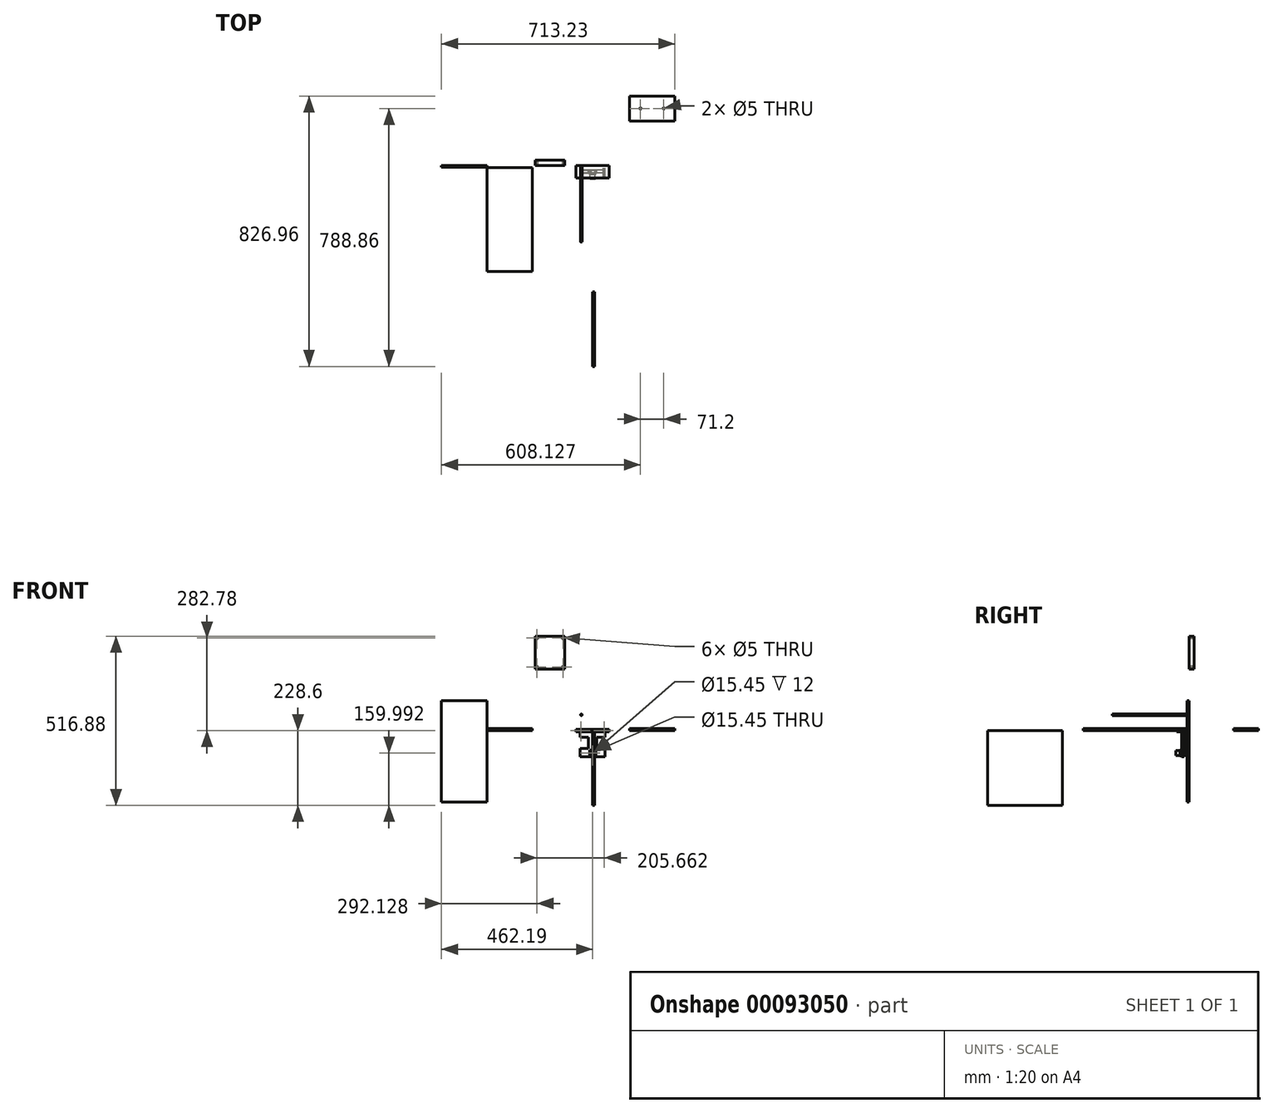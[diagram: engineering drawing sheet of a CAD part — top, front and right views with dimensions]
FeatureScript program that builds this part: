
annotation { "Feature Type Name" : "Feature", "Feature Type Description" : "" }
export const myFeature = defineFeature(function(context is Context, id is Id, definition is map)
    precondition{}
    {
        {
            var Q0;
            Q0=qCreatedBy(makeId("Front.planeOp"),FACE);
            var sketch = newSketch(context, id + "F0", { "sketchPlane" : qUnion([Q0])});
            skLineSegment(sketch, "E0.bottom", {"start": v(-50.8, -4) * mm, "end": v(50.8, -4) * mm});
            skLineSegment(sketch, "E0.top", {"start": v(-50.8, 4) * mm, "end": v(50.8, 4) * mm});
            skLineSegment(sketch, "E0.left", {"start": v(-50.8, -4) * mm, "end": v(-50.8, 4) * mm});
            skLineSegment(sketch, "E0.right", {"start": v(50.8, -4) * mm, "end": v(50.8, 4) * mm});
            skPoint(sketch, "E0.middle", {"position": v(0, 0) * mm});
            skCircle(sketch, "E1", {"center": v(-35.6, 0) * mm, "radius": 2.5 * mm});
            skCircle(sketch, "E2", {"center": v(35.6, 0) * mm, "radius": 2.5 * mm});
            skSolve(sketch);
        }
        {
            var Q0;
            Q0=qSketchRegion(id+"F0",true);
            extrude(context, id + "F1", {"entities" : qUnion([Q0]), "depth" : 38.1 * mm});
        }
        {
            var Q0;
            Q0=qCreatedBy(makeId("Front.planeOp"),FACE);
            var sketch = newSketch(context, id + "F2", { "sketchPlane" : qUnion([Q0])});
            skCircle(sketch, "E3", {"center": v(-34.4, 48.2) * mm, "radius": 2.5 * mm});
            skSolve(sketch);
        }
        {
            var Q0;
            Q0=makeQuery(id+"F2.imprint","IMPRINT",FACE,{"disambiguationData":[TD([[makeQuery(id+"F2.imprint","IMPRINT",EDGE,{"derivedFrom":sQuery(id+"F2.wireOp",EDGE,"E3")}),1.0]])]});
            extrude(context, id + "F3", {"entities" : qUnion([Q0]), "depth" : 228.6 * mm + 6 * mm});
        }
        {
            var Q0;
            Q0=qCreatedBy(makeId("Right.planeOp"),FACE);
            var sketch = newSketch(context, id + "F4", { "sketchPlane" : qUnion([Q0])});
            skLineSegment(sketch, "E4.bottom", {"start": v(-386.33, 0) * mm, "end": v(-691.13, 0) * mm});
            skLineSegment(sketch, "E4.top", {"start": v(-386.33, -304.8) * mm, "end": v(-691.13, -304.8) * mm});
            skLineSegment(sketch, "E4.left", {"start": v(-386.33, 0) * mm, "end": v(-386.33, -304.8) * mm});
            skLineSegment(sketch, "E4.right", {"start": v(-691.13, 0) * mm, "end": v(-691.13, -304.8) * mm});
            skPoint(sketch, "E4.middle", {"position": v(-538.73, -152.4) * mm});
            skLineSegment(sketch, "E5.bottom", {"start": v(-386.33, -228.6) * mm, "end": v(-614.93, -228.6) * mm});
            skLineSegment(sketch, "E5.top", {"start": v(-386.33, 0) * mm, "end": v(-614.93, 0) * mm});
            skLineSegment(sketch, "E5.left", {"start": v(-386.33, -228.6) * mm, "end": v(-386.33, 0) * mm});
            skLineSegment(sketch, "E5.right", {"start": v(-614.93, -228.6) * mm, "end": v(-614.93, 0) * mm});
            skPoint(sketch, "E5.middle", {"position": v(-500.63, -114.3) * mm});
            skSolve(sketch);
        }
        {
            var Q0;
            Q0=makeQuery(id+"F4.imprint","IMPRINT",FACE,{"disambiguationData":[TD([[makeQuery(id+"F4.imprint","IMPRINT",EDGE,{"derivedFrom":sQuery(id+"F4.wireOp",EDGE,"E4.bottom")}),1.0]])]});
            extrude(context, id + "F5", {"entities" : qUnion([Q0]), "depth" : 6 * mm});
        }
        {
            var Q0;
            Q0=qCreatedBy(makeId("Front.planeOp"),FACE);
            var sketch = newSketch(context, id + "F6", { "sketchPlane" : qUnion([Q0])});
            skLineSegment(sketch, "E6.bottom", {"start": v(-462.2, 91.62) * mm, "end": v(-323.2, 91.62) * mm});
            skLineSegment(sketch, "E6.top", {"start": v(-462.2, -219.18) * mm, "end": v(-323.2, -219.18) * mm});
            skLineSegment(sketch, "E6.left", {"start": v(-462.2, 91.62) * mm, "end": v(-462.2, -219.18) * mm});
            skLineSegment(sketch, "E6.right", {"start": v(-323.2, 91.62) * mm, "end": v(-323.2, -219.18) * mm});
            skPoint(sketch, "E6.middle", {"position": v(-392.7, -63.78) * mm});
            skSolve(sketch);
        }
        {
            var Q0;
            Q0 = qSketchRegion(id + "F6", true);
            extrude(context, id + "F7", {"entities" : qUnion([Q0]), "depth" : 6 * mm});
        }
        {
            var Q0;
            Q0=qCreatedBy(makeId("Top.planeOp"),FACE);
            var sketch = newSketch(context, id + "F8", { "sketchPlane" : qUnion([Q0])});
            skLineSegment(sketch, "E7.bottom", {"start": v(-184.06, -7.03) * mm, "end": v(-323.06, -7.03) * mm});
            skLineSegment(sketch, "E7.top", {"start": v(-184.06, -323.83) * mm, "end": v(-323.06, -323.83) * mm});
            skLineSegment(sketch, "E7.left", {"start": v(-184.06, -7.03) * mm, "end": v(-184.06, -323.83) * mm});
            skLineSegment(sketch, "E7.right", {"start": v(-323.06, -7.03) * mm, "end": v(-323.06, -323.83) * mm});
            skPoint(sketch, "E7.middle", {"position": v(-253.56, -165.43) * mm});
            skSolve(sketch);
        }
        {
            var Q0;
            Q0 = qSketchRegion(id + "F8", true);
            extrude(context, id + "F9", {"entities" : qUnion([Q0]), "depth" : 6 * mm});
        }
        {
            var Q0;
            Q0=qCreatedBy(makeId("Top.planeOp"),FACE);
            var sketch = newSketch(context, id + "F10", { "sketchPlane" : qUnion([Q0])});
            skLineSegment(sketch, "E8.bottom", {"start": v(251.04, 135.83) * mm, "end": v(112.04, 135.83) * mm});
            skLineSegment(sketch, "E8.top", {"start": v(251.04, 212.03) * mm, "end": v(112.04, 212.03) * mm});
            skLineSegment(sketch, "E8.left", {"start": v(251.04, 135.83) * mm, "end": v(251.04, 212.03) * mm});
            skLineSegment(sketch, "E8.right", {"start": v(112.04, 135.83) * mm, "end": v(112.04, 212.03) * mm});
            skPoint(sketch, "E8.middle", {"position": v(181.54, 173.93) * mm});
            skCircle(sketch, "E9", {"center": v(145.94, 173.93) * mm, "radius": 2.5 * mm});
            skCircle(sketch, "E10", {"center": v(217.14, 173.93) * mm, "radius": 2.5 * mm});
            skSolve(sketch);
        }
        {
            var Q0;
            Q0 = qSketchRegion(id + "F10", true);
            extrude(context, id + "F11", {"entities" : qUnion([Q0]), "depth" : 6 * mm});
        }
        {
            var Q0;
            Q0=qCreatedBy(makeId("Front.planeOp"),FACE);
            var sketch = newSketch(context, id + "F12", { "sketchPlane" : qUnion([Q0])});
            skLineSegment(sketch, "E11.bottom", {"start": v(-85.56, 188.28) * mm, "end": v(-175.56, 188.28) * mm});
            skLineSegment(sketch, "E11.top", {"start": v(-85.56, 288.28) * mm, "end": v(-175.56, 288.28) * mm});
            skLineSegment(sketch, "E11.left", {"start": v(-85.56, 188.28) * mm, "end": v(-85.56, 288.28) * mm});
            skLineSegment(sketch, "E11.right", {"start": v(-175.56, 188.28) * mm, "end": v(-175.56, 288.28) * mm});
            skPoint(sketch, "E11.middle", {"position": v(-130.56, 238.28) * mm});
            skCircle(sketch, "E12", {"center": v(-170.06, 282.78) * mm, "radius": 2.5 * mm});
            skCircle(sketch, "E13", {"center": v(-91.06, 282.78) * mm, "radius": 2.5 * mm});
            skCircle(sketch, "E14", {"center": v(-91.06, 193.78) * mm, "radius": 2.5 * mm});
            skCircle(sketch, "E15", {"center": v(-170.06, 193.78) * mm, "radius": 2.5 * mm});
            skSolve(sketch);
        }
        {
            var Q0;
            Q0=makeQuery(id+"F12.imprint","IMPRINT",FACE,{"disambiguationData":[TD([[makeQuery(id+"F12.imprint","IMPRINT",EDGE,{"derivedFrom":sQuery(id+"F12.wireOp",EDGE,"E11.bottom")}),-1.0]])]});
            extrude(context, id + "F13", {"entities" : qUnion([Q0]), "operationType" : NewBodyOperationType.ADD, "oppositeDirection" : true, "depth" : 16 * mm});
        }
        {
            var Q0;
            Q0=makeQuery(id+"F12.imprint","IMPRINT",FACE,{"disambiguationData":[TD([[makeQuery(id+"F12.imprint","IMPRINT",EDGE,{"derivedFrom":sQuery(id+"F12.wireOp",EDGE,"E12")}),1.0]])]});
            var Q1;
            Q1=makeQuery(id+"F12.imprint","IMPRINT",FACE,{"disambiguationData":[TD([[makeQuery(id+"F12.imprint","IMPRINT",EDGE,{"derivedFrom":sQuery(id+"F12.wireOp",EDGE,"E13")}),1.0]])]});
            var Q2;
            Q2=makeQuery(id+"F12.imprint","IMPRINT",FACE,{"disambiguationData":[TD([[makeQuery(id+"F12.imprint","IMPRINT",EDGE,{"derivedFrom":sQuery(id+"F12.wireOp",EDGE,"E14")}),1.0]])]});
            var Q3;
            Q3=makeQuery(id+"F12.imprint","IMPRINT",FACE,{"disambiguationData":[TD([[makeQuery(id+"F12.imprint","IMPRINT",EDGE,{"derivedFrom":sQuery(id+"F12.wireOp",EDGE,"E15")}),1.0]])]});
            extrude(context, id + "F14", {"entities" : qUnion([Q0, Q1, Q2, Q3]), "oppositeDirection" : true, "depth" : 16 * mm});
        }
        {
            var Q0;
            Q0=makeQuery(id+"F1.opExtrude","SWEPT_FACE",FACE,{"disambiguationData":[OSD([sQuery(id+"F0.wireOp",EDGE,"E0.bottom")])]});
            var sketch = newSketch(context, id + "F15", { "sketchPlane" : qUnion([Q0])});
            skLineSegment(sketch, "E16", {"start": v(-50.8, 38.1) * mm, "end": v(50.8, 0) * mm, "construction": true});
            skLineSegment(sketch, "E17", {"start": v(50.8, 38.1) * mm, "end": v(-50.8, 0) * mm, "construction": true});
            skPoint(sketch, "E18", {"position": v(0, 19.05) * mm});
            skLineSegment(sketch, "E19.bottom", {"start": v(38.1, 15.05) * mm, "end": v(-38.1, 15.05) * mm});
            skLineSegment(sketch, "E19.top", {"start": v(38.1, 23.05) * mm, "end": v(-38.1, 23.05) * mm});
            skLineSegment(sketch, "E19.left", {"start": v(38.1, 15.05) * mm, "end": v(38.1, 23.05) * mm});
            skLineSegment(sketch, "E19.right", {"start": v(-38.1, 15.05) * mm, "end": v(-38.1, 23.05) * mm});
            skSolve(sketch);
        }
        {
            var Q0;
            Q0 = qSketchRegion(id + "F15", true);
            extrude(context, id + "F16", {"entities" : qUnion([Q0]), "operationType" : NewBodyOperationType.ADD, "depth" : 76.2 * mm});
        }
        {
            var Q0;
            Q0=makeQuery(id+"F16.opExtrude","SWEPT_FACE",FACE,{"disambiguationData":[OSD([sQuery(id+"F15.wireOp",EDGE,"E19.bottom")])]});
            var sketch = newSketch(context, id + "F17", { "sketchPlane" : qUnion([Q0])});
            skLineSegment(sketch, "E20.bottom", {"start": v(-38.1, -21.02) * mm, "end": v(-12.7, -21.02) * mm});
            skLineSegment(sketch, "E20.top", {"start": v(-38.1, -54) * mm, "end": v(-12.7, -54) * mm});
            skLineSegment(sketch, "E20.left", {"start": v(-38.1, -21.02) * mm, "end": v(-38.1, -54) * mm});
            skLineSegment(sketch, "E20.right", {"start": v(-12.7, -21.02) * mm, "end": v(-12.7, -54) * mm});
            skLineSegment(sketch, "E21.bottom", {"start": v(38.1, -21.02) * mm, "end": v(12.7, -21.02) * mm});
            skLineSegment(sketch, "E21.top", {"start": v(38.1, -54.7) * mm, "end": v(12.7, -54.7) * mm});
            skLineSegment(sketch, "E21.left", {"start": v(38.1, -21.02) * mm, "end": v(38.1, -54.7) * mm});
            skLineSegment(sketch, "E21.right", {"start": v(12.7, -21.02) * mm, "end": v(12.7, -54.7) * mm});
            skPoint(sketch, "E22", {"position": v(38.1, -21.02) * mm});
            skLineSegment(sketch, "E23.bottom", {"start": v(9.4, -78) * mm, "end": v(-9.4, -78) * mm});
            skLineSegment(sketch, "E23.top", {"start": v(9.4, -59.22) * mm, "end": v(-9.4, -59.22) * mm});
            skLineSegment(sketch, "E23.left", {"start": v(9.4, -78) * mm, "end": v(9.4, -59.22) * mm});
            skLineSegment(sketch, "E23.right", {"start": v(-9.4, -78) * mm, "end": v(-9.4, -59.22) * mm});
            skPoint(sketch, "E23.middle", {"position": v(0, -68.6) * mm});
            skCircle(sketch, "E24", {"center": v(0, -68.6) * mm, "radius": 7.72 * mm});
            skCircle(sketch, "E25", {"center": v(0, -68.6) * mm, "radius": 5.45 * mm});
            skSolve(sketch);
        }
        {
            var Q0;
            Q0=makeQuery(id+"F17.imprint","IMPRINT",FACE,{"disambiguationData":[TD([[makeQuery(id+"F17.imprint","IMPRINT",EDGE,{"derivedFrom":sQuery(id+"F17.wireOp",EDGE,"E20.bottom")}),-1.0]])]});
            var Q1;
            Q1=makeQuery(id+"F17.imprint","IMPRINT",FACE,{"disambiguationData":[TD([[makeQuery(id+"F17.imprint","IMPRINT",EDGE,{"derivedFrom":sQuery(id+"F17.wireOp",EDGE,"E21.bottom")}),1.0]])]});
            extrude(context, id + "F18", {"entities" : qUnion([Q0, Q1]), "operationType" : NewBodyOperationType.REMOVE, "endBound" : BoundingType.THROUGH_ALL, "oppositeDirection" : true, "depth" : 25.4 * mm});
        }
        {
            var Q0;
            Q0=makeQuery(id+"F17.imprint","IMPRINT",FACE,{"disambiguationData":[TD([[makeQuery(id+"F17.imprint","IMPRINT",EDGE,{"derivedFrom":sQuery(id+"F17.wireOp",EDGE,"E23.bottom")}),-1.0]])]});
            extrude(context, id + "F19", {"entities" : qUnion([Q0]), "oppositeDirection" : true, "depth" : 12 * mm});
        }
        {
            var Q0;
            Q0=makeQuery(id+"F17.imprint","IMPRINT",FACE,{"disambiguationData":[TD([[makeQuery(id+"F17.imprint","IMPRINT",EDGE,{"derivedFrom":sQuery(id+"F17.wireOp",EDGE,"E25")}),1.0]])]});
            var Q1;
            Q1=makeQuery(id+"F17.imprint","IMPRINT",FACE,{"disambiguationData":[TD([[makeQuery(id+"F17.imprint","IMPRINT",EDGE,{"derivedFrom":sQuery(id+"F17.wireOp",EDGE,"E24")}),1.0]])]});
            extrude(context, id + "F20", {"entities" : qUnion([Q0, Q1]), "oppositeDirection" : true, "depth" : 25.4 * mm});
        }
        {
            var Q0;
            Q0=makeQuery(id+"F17.imprint","IMPRINT",FACE,{"disambiguationData":[TD([[makeQuery(id+"F17.imprint","IMPRINT",EDGE,{"derivedFrom":sQuery(id+"F17.wireOp",EDGE,"E24")}),1.0]])]});
            extrude(context, id + "F21", {"entities" : qUnion([Q0]), "operationType" : NewBodyOperationType.REMOVE, "depth" : 25.4 * mm, "hasSecondDirection" : true, "secondDirectionOppositeDirection" : true, "secondDirectionDepth" : 10.16 * mm});
        }
    });
